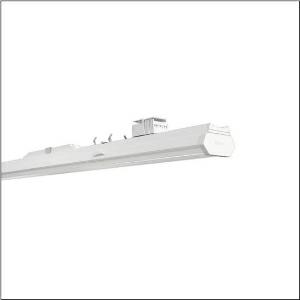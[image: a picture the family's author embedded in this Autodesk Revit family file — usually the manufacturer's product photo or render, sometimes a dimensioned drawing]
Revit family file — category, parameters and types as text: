
# Revit family: licross_r__11_protected_mo_51tp12dn49xfd_6896
name_source: partatom
category: Lighting Fixtures
units: mm (PartAtom-declared; Revit-internal decimal feet)

## family parameters
Cut with Voids When Loaded = No
Host = Face
Light Source = No
Part Type = Normal
Room Calculation Point = No
Round Connector Dimension = Use Diameter
Shared = No

## types (1)
- --- (1 x LED, 1410 lm, 10 W, 4000K)
    Apparent Load = 10 VA
    CIE Flux Codes = 73 92 98 99 100
    Color Rendering = 80
    Color Temperature = 4000K
    Default Elevation = 1800 mm
    Description = Licross® 11 Protected MOluminaire insert, length: 1.500mm, width: 90mm, height: 101mm, LED rated luminous flux: 9.020lm, light colour: 840, control gear: DALI 2, control gear: ECG DALI, with plug, 6-pole, with phase selection, mains connection: 220..240V, AC/DC, 0/50..60Hz, for central battery installations according to DIN EN 60598-2-22, for emergency light function, without changeover relay, halogen-free wiring, primary optical cover: cover, of PMMA, light emission: direct with ceiling illumination distribution, protection rating (complete): IP64, insulation class (complete): insulation class I (protective earthing), certification: CE, ENEC, VDE, protection symbol: D if used in an environment without relevant dust loads with corresponding accessories, permissible ambient temperature for indoor applications: -25..+40°C, standard: EN 60598-2-22, reducing of maximum allowable ambient temperature of 5°C with ceiling mounting, corresponds to IFS (International Featured Standards) requirements for safety and quality in the food industry, packaging unit: 1 piece
    Height = 92 mm
    Lamp = 1 x LED
    Lamp Light Flux = 1410 lm
    Lamp Power = 10 W
    Lamp count = 1
    Length = 1500 mm
    Luminous efficacy = 141 lm/W
    Manufacturer = Siteco
    ModVariant = No
    Model = 51TP12DN49XFD
    Mounting Place = Ceiling
    Mounting Type = Pendant
    Number of Poles = 1
    OnlyDefault = Yes
    Power Factor = 1
    Product Name = Licross® 11 Protected MO
    Product group = luminaire insert
    ProductGroupID = 902
    Protection Class = Protection class I
    Protection Degree = IP 64
    RLX_Detail_Level = 1
    RlxData = <blob elided: 24337 chars, md5=f70e7ef7>
    Socket = socket
    Standby Power = 0 W
    System Light Flux = 1410 lm
    System Power = 10 W
    Type Comments = : DC mode (central or group accumulator) initial emergency light level
    Type Image = l_1256148.jpg
    URL = http://relux.com
    VarID = @adj_134709
    Voltage = 0 V
    Weight = 0.00 kg
    Width = 88 mm

## geometry (parser evidence)
native form markers: Blend x4, Sweep x10
no freeform markers — native parametric forms only
